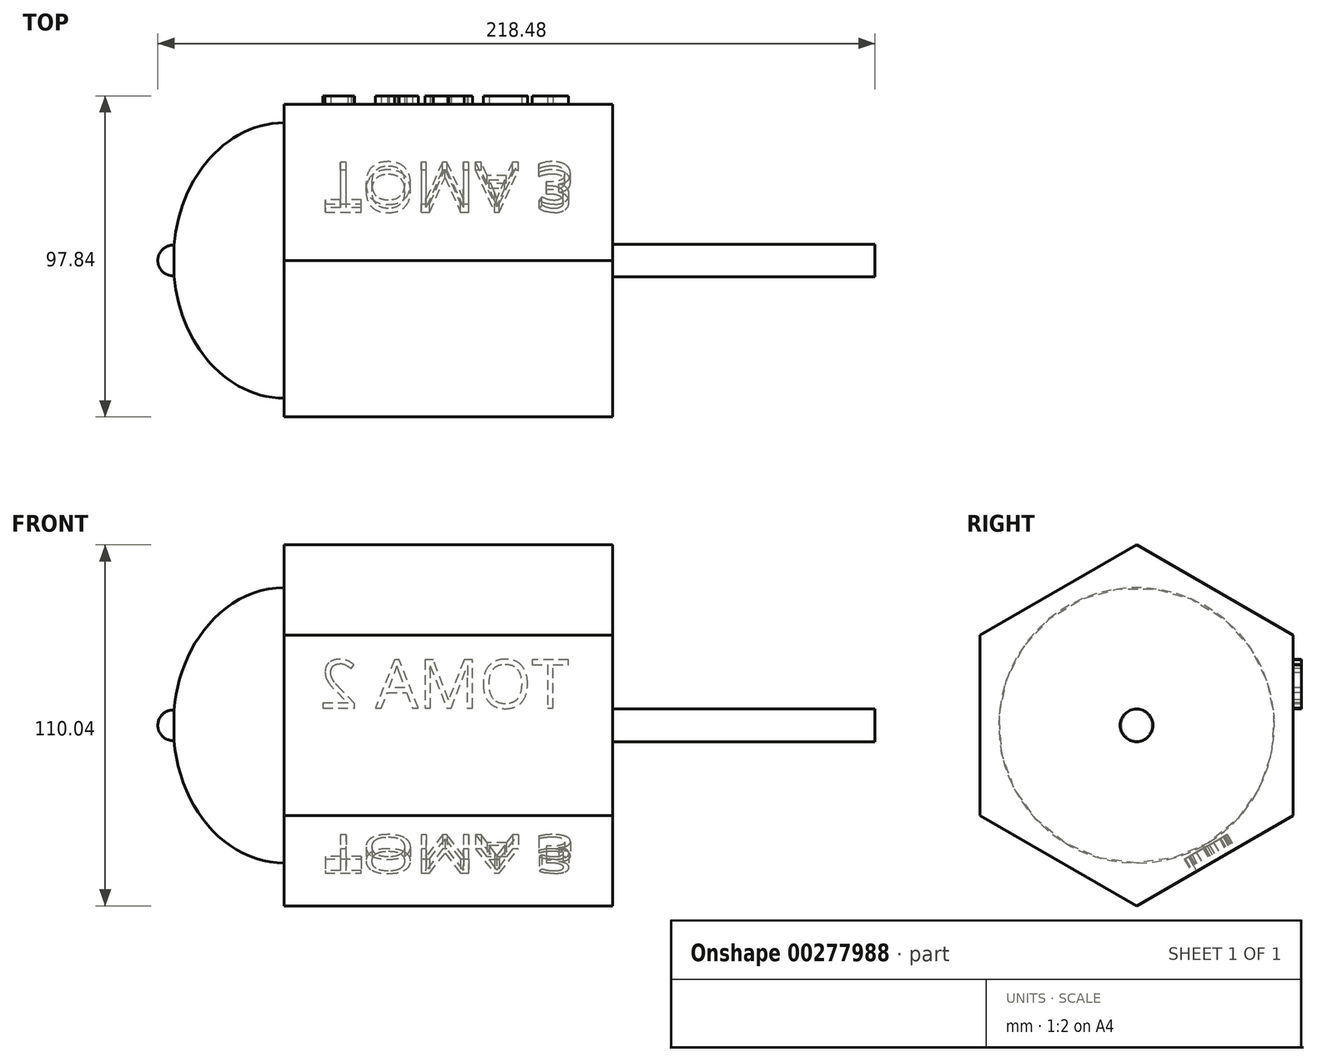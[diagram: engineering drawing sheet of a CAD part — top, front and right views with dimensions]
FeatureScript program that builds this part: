
annotation { "Feature Type Name" : "Feature", "Feature Type Description" : "" }
export const myFeature = defineFeature(function(context is Context, id is Id, definition is map)
    precondition{}
    {
        {
            var Q0;
            Q0=qCreatedBy(makeId("Right.planeOp"),FACE);
            var sketch = newSketch(context, id + "F0", { "sketchPlane" : qUnion([Q0])});
            skCircle(sketch, "E0.cCircle", {"center": v(0, 0) * mm, "radius": 47.65 * mm, "construction": true});
            skLineSegment(sketch, "E0.0", {"start": v(47.65, 27.51) * mm, "end": v(47.65, -27.51) * mm});
            skLineSegment(sketch, "E0.1", {"start": v(47.65, -27.51) * mm, "end": v(0, -55.02) * mm});
            skLineSegment(sketch, "E0.2", {"start": v(0, -55.02) * mm, "end": v(-47.65, -27.51) * mm});
            skLineSegment(sketch, "E0.3", {"start": v(-47.65, -27.51) * mm, "end": v(-47.65, 27.51) * mm});
            skLineSegment(sketch, "E0.4", {"start": v(-47.65, 27.51) * mm, "end": v(0, 55.02) * mm});
            skLineSegment(sketch, "E0.5", {"start": v(0, 55.02) * mm, "end": v(47.65, 27.51) * mm});
            skPoint(sketch, "E0.0.midPoint", {"position": v(47.65, 0) * mm});
            skSolve(sketch);
        }
        {
            var Q0;
            Q0 = qSketchRegion(id + "F0", true);
            extrude(context, id + "F1", {"entities" : qUnion([Q0]), "depth" : 100 * mm});
        }
        {
            var Q0;
            Q0=makeQuery(id+"F1.opExtrude","CAP_FACE",FACE,{"disambiguationData":[OSD([sQuery(id+"F0.wireOp",EDGE,"E0.0"),sQuery(id+"F0.wireOp",EDGE,"E0.1"),sQuery(id+"F0.wireOp",EDGE,"E0.2"),sQuery(id+"F0.wireOp",EDGE,"E0.3"),sQuery(id+"F0.wireOp",EDGE,"E0.4"),sQuery(id+"F0.wireOp",EDGE,"E0.5")])],"isStart":false});
            var sketch = newSketch(context, id + "F2", { "sketchPlane" : qUnion([Q0])});
            skCircle(sketch, "E1", {"center": v(0, 0) * mm, "radius": 5 * mm});
            skSolve(sketch);
        }
        {
            var Q0;
            Q0 = qSketchRegion(id + "F2", true);
            extrude(context, id + "F3", {"entities" : qUnion([Q0]), "operationType" : NewBodyOperationType.ADD, "depth" : 80 * mm});
        }
        {
            var Q0;
            Q0=qCreatedBy(makeId("Front.planeOp"),FACE);
            var sketch = newSketch(context, id + "F4", { "sketchPlane" : qUnion([Q0])});
            skLineSegment(sketch, "E2", {"start": v(0, 0) * mm, "end": v(-33.8, 0) * mm, "construction": true});
            skLineSegment(sketch, "E3", {"start": v(0, 0) * mm, "end": v(0, 41.97) * mm, "construction": true});
            skEllipticalArc(sketch, "E4", {});
            skLineSegment(sketch, "E5", {"start": v(-33.8, 0) * mm, "end": v(-38.48, 0) * mm, "construction": true});
            skArc(sketch, "E6", {"start": v(-38.48, 0) * mm, "mid": v(-37.03, 3.38) * mm, "end": v(-33.59, 4.67) * mm});
            skLineSegment(sketch, "E7", {"start": v(-38.48, 0) * mm, "end": v(0, 0) * mm});
            skLineSegment(sketch, "E8", {"start": v(0, 41.97) * mm, "end": v(0, 0) * mm});
            skLineSegment(sketch, "E9", {"start": v(0, 0) * mm, "end": v(-55.2, 0) * mm, "construction": true});
            skPoint(sketch, "E9.endSnap0", {"position": v(-19.24, 0) * mm});
            const initialGuessF4  = {"E4": [0, 0, -1, 0, 0.03380007967197671, 0.04196638800000001, 4.71238898038469, 6.171563597285034]};
            skSetInitialGuess(sketch, initialGuessF4);
            skSolve(sketch);
        }
        {
            var Q0;
            Q0=makeQuery(id+"F4.imprint","IMPRINT",FACE,{"disambiguationData":[TD([[makeQuery(id+"F4.imprint","IMPRINT",EDGE,{"derivedFrom":sQuery(id+"F4.wireOp",EDGE,"E4")}),1.0]])]});
            var Q1;
            Q1=sQuery(id+"F4.wireOp",EDGE,"E9");
            revolve(context, id + "F5", {"operationType" : NewBodyOperationType.ADD, "entities" : qUnion([Q0]), "axis" : qUnion([Q1]), "revolveType" : RevolveType.FULL});
        }
        {
            var Q0;
            Q0=makeQuery(id+"F1.opExtrude","SWEPT_FACE",FACE,{"disambiguationData":[OSD([sQuery(id+"F0.wireOp",EDGE,"E0.0")])]});
            var sketch = newSketch(context, id + "F6", { "sketchPlane" : qUnion([Q0])});
            skText(sketch, "E10", { "text": "TOMA 2", "fontName": "OpenSans-Regular.ttf"});
            const initialGuessF6  = {"E10": [-0.08675, 0.00526, 1, 0, 0.01479]};
            skSetInitialGuess(sketch, initialGuessF6);
            skSolve(sketch);
        }
        {
            var Q0;
            Q0 = qSketchRegion(id + "F6", true);
            extrude(context, id + "F7", {"entities" : qUnion([Q0]), "operationType" : NewBodyOperationType.ADD, "depth" : 2.54 * mm});
        }
        {
            var Q0;
            Q0=makeQuery(id+"F1.opExtrude","SWEPT_FACE",FACE,{"disambiguationData":[OSD([sQuery(id+"F0.wireOp",EDGE,"E0.1")])]});
            var sketch = newSketch(context, id + "F8", { "sketchPlane" : qUnion([Q0])});
            skText(sketch, "E11", { "text": "TOMA 3\n", "fontName": "OpenSans-Regular.ttf"});
            const initialGuessF8  = {"E11": [0.01235, -0.00711, 1, 0, 0.0148]};
            skSetInitialGuess(sketch, initialGuessF8);
            skSolve(sketch);
        }
        {
            var Q0;
            Q0 = qSketchRegion(id + "F8", true);
            extrude(context, id + "F9", {"entities" : qUnion([Q0]), "operationType" : NewBodyOperationType.REMOVE, "oppositeDirection" : true, "depth" : 5 * mm});
        }
    });
